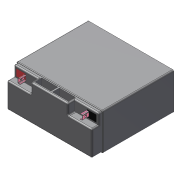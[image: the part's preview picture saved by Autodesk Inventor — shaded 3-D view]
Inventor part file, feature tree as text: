
AUTODESK INVENTOR PART (.ipt)
format: ipt  version: 2012 (Build 160160000, 160)  size: 215,040 bytes
history: native  units: mm (DEFAULTED — no unit token found)
features: extrude x8, sketch x8, fillet x4, mirror x2, plane x1
ambient origin geometry x8: Origin, YZ Plane, XZ Plane, XY Plane, X Axis, Y Axis, Z Axis, Center Point
bodies: Solid1 (feature_tree)
feature tree (23):
  extrude  "Extrusion1"  Depth=76.2mm
  extrude  "Extrusion2"  Depth=21.082mm TaperAngle=0.0deg
  extrude  "Extrusion3"  Depth=21.336mm
  fillet  "Fillet1"  Radius=14.224mm
  fillet  "Fillet2"  Radius=2.54mm
  fillet  "Fillet3"  Radius=1.27mm
  fillet  "Fillet4"  Radius=2.54mm
  extrude  "Extrusion4"  Depth=0.254mm TaperAngle=0.0deg
  extrude  "Extrusion5"  Depth=12.7mm TaperAngle=0.0deg
  extrude  "Extrusion6"  Depth=12.7mm TaperAngle=0.0deg
  plane  "Work Plane1"
  mirror  "Mirror1"
  mirror  "Mirror2"
  extrude  "Extrusion7"  Depth=20.32mm
  extrude  "Extrusion8"  Depth=19.558mm TaperAngle=0.0deg
  sketch  "Sketch1"  dims[d0=177.8mm d1=76.2mm]
  sketch  "Sketch2"  dims[d2=146.05mm d3=0.0mm d4=21.082mm d5=0.0mm]
  sketch  "Sketch3"  dims[d6=49.276mm d7=21.336mm d8=14.224mm d9=0.0mm d10=2.54mm d11=1.27mm d12=2.54mm]
  sketch  "Sketch4"  dims[d13=2.54mm d14=0.254mm d15=0.0mm]
  sketch  "Sketch5"  dims[d16=1.524mm d17=12.7mm d18=0.0mm]
  sketch  "Sketch6"  dims[d19=5.08mm d20=12.7mm d21=0.0mm]
  sketch  "Sketch7"  dims[d22=20.32mm d23=20.32mm]
  sketch  "Sketch8"  dims[d24=63.5mm d25=19.558mm d26=0.0mm d27=33.02mm d28=3.048mm d29=19.05mm d30=0.0mm]
